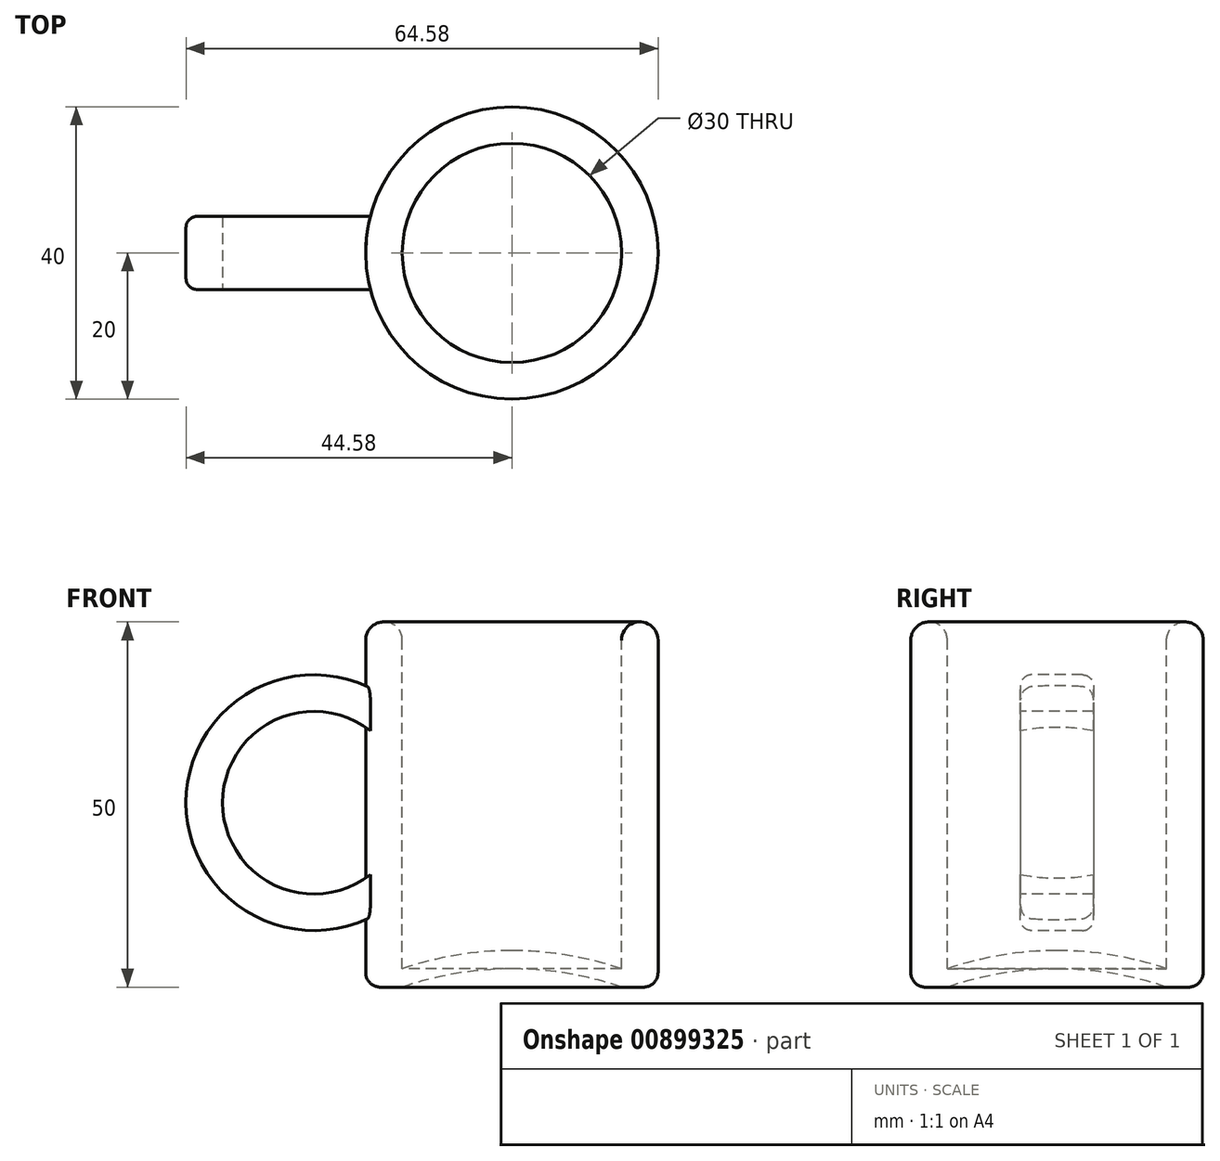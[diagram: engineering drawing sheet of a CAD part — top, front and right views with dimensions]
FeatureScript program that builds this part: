
annotation { "Feature Type Name" : "Feature", "Feature Type Description" : "" }
export const myFeature = defineFeature(function(context is Context, id is Id, definition is map)
    precondition{}
    {
        {
            var Q0;
            Q0=qCreatedBy(makeId("Front.planeOp"),FACE);
            var sketch = newSketch(context, id + "F0", { "sketchPlane" : qUnion([Q0])});
            skLineSegment(sketch, "E0.bottom", {"start": v(0, 0) * mm, "end": v(5, 0) * mm, "construction": true});
            skLineSegment(sketch, "E0.top", {"start": v(0, 47.5) * mm, "end": v(5, 47.5) * mm, "construction": true});
            skLineSegment(sketch, "E0.left", {"start": v(0, 0) * mm, "end": v(0, 47.5) * mm, "construction": true});
            skLineSegment(sketch, "E0.right", {"start": v(40, 0) * mm, "end": v(40, 47.5) * mm});
            skLineSegment(sketch, "E1", {"start": v(5, 47.5) * mm, "end": v(5, 2.5) * mm, "construction": true});
            skLineSegment(sketch, "E2", {"start": v(35, 47.5) * mm, "end": v(35, 2.5) * mm});
            skArc(sketch, "E3", {"start": v(35, 0) * mm, "mid": v(27.6, 1.87) * mm, "end": v(20, 2.5) * mm});
            skLineSegment(sketch, "E4", {"start": v(5, 47.5) * mm, "end": v(20, 47.5) * mm, "construction": true});
            skLineSegment(sketch, "E5", {"start": v(35, 47.5) * mm, "end": v(40, 47.5) * mm});
            skLineSegment(sketch, "E6", {"start": v(35, 0) * mm, "end": v(40, 0) * mm});
            skLineSegment(sketch, "E7", {"start": v(5, 0) * mm, "end": v(20, 0) * mm, "construction": true});
            skArc(sketch, "E8", {"start": v(0, 47.5) * mm, "mid": v(2.5, 50) * mm, "end": v(5, 47.5) * mm, "construction": true});
            skArc(sketch, "E9", {"start": v(35, 47.5) * mm, "mid": v(37.5, 50) * mm, "end": v(40, 47.5) * mm});
            skLineSegment(sketch, "E10", {"start": v(20, 0) * mm, "end": v(20, 2.5) * mm, "construction": true});
            skLineSegment(sketch, "E11", {"start": v(20, 0) * mm, "end": v(35, 0) * mm, "construction": true});
            skLineSegment(sketch, "E12", {"start": v(20, 2.5) * mm, "end": v(20, 5) * mm});
            skLineSegment(sketch, "E13", {"start": v(20, 47.5) * mm, "end": v(35, 47.5) * mm, "construction": true});
            skArc(sketch, "E14", {"start": v(20, 2.5) * mm, "mid": v(12.4, 1.87) * mm, "end": v(5, 0) * mm, "construction": true});
            skLineSegment(sketch, "E15", {"start": v(20, 2.5) * mm, "end": v(20, 2.5) * mm});
            skArc(sketch, "E16", {"start": v(35, 2.5) * mm, "mid": v(27.6, 4.37) * mm, "end": v(20, 5) * mm});
            skLineSegment(sketch, "E17", {"start": v(5, 2.5) * mm, "end": v(5, 2.5) * mm});
            skArc(sketch, "E18", {"start": v(20, 5) * mm, "mid": v(12.4, 4.37) * mm, "end": v(5, 2.5) * mm});
            skLineSegment(sketch, "E19", {"start": v(5, 2.5) * mm, "end": v(5, 0) * mm, "construction": true});
            skLineSegment(sketch, "E20", {"start": v(35, 2.5) * mm, "end": v(35, 0) * mm});
            skLineSegment(sketch, "E21", {"start": v(20, 5) * mm, "end": v(20, 5) * mm});
            skLineSegment(sketch, "E22", {"start": v(20, 5) * mm, "end": v(20, 47.5) * mm, "construction": true});
            skSolve(sketch);
        }
        {
            var Q0;
            Q0 = qSketchRegion(id + "F0", true);
            var Q1;
            Q1=sQuery(id+"F0.wireOp",EDGE,"E10");
            revolve(context, id + "F1", {"surfaceOperationType" : NewSurfaceOperationType.NEW, "entities" : qUnion([Q0]), "axis" : qUnion([Q1]), "revolveType" : RevolveType.FULL, "oppositeDirection" : true});
        }
        {
            var Q0;
            Q0=qCreatedBy(makeId("Front.planeOp"),FACE);
            var sketch = newSketch(context, id + "F2", { "sketchPlane" : qUnion([Q0])});
            skPoint(sketch, "E23.0", {"position": v(0, 0) * mm});
            skLineSegment(sketch, "E24", {"start": v(40, 47.5) * mm, "end": v(40, 0) * mm});
            skLineSegment(sketch, "E25", {"start": v(0, 0) * mm, "end": v(0, 47.5) * mm, "construction": true});
            skLineSegment(sketch, "E26", {"start": v(1.5, 0) * mm, "end": v(1.5, 10) * mm, "construction": true});
            skLineSegment(sketch, "E27", {"start": v(1.5, 47.5) * mm, "end": v(0, 47.5) * mm});
            skLineSegment(sketch, "E28", {"start": v(1.5, 40.5) * mm, "end": v(1.5, 47.5) * mm, "construction": true});
            skLineSegment(sketch, "E29", {"start": v(1.5, 34.34) * mm, "end": v(1.5, 40.5) * mm});
            skLineSegment(sketch, "E30", {"start": v(1.5, 16.16) * mm, "end": v(1.5, 34.34) * mm, "construction": true});
            skLineSegment(sketch, "E31", {"start": v(1.5, 10) * mm, "end": v(1.5, 16.16) * mm});
            skArc(sketch, "E32", {"start": v(1.5, 40.5) * mm, "mid": v(-24.58, 25.25) * mm, "end": v(1.5, 10) * mm});
            skArc(sketch, "E33", {"start": v(1.5, 34.34) * mm, "mid": v(-19.58, 25.25) * mm, "end": v(1.5, 16.16) * mm});
            skSolve(sketch);
        }
        {
            var Q0;
            {var subQ0=sQuery(id+"F2.wireOp",EDGE,"zNirZaeI-mv0y-j9wX-MBT8-WwsDXe8e62ri");Q0=makeQuery(id+"F2.imprint","IMPRINT",FACE,{"disambiguationData":[TD([[makeQuery(id+"F2.imprint","IMPRINT",EDGE,{"derivedFrom":subQ0}),1.0]])]});}
            var Q1;
            Q1=makeQuery(id+"F2.imprint","IMPRINT",FACE,{"disambiguationData":[TD([[makeQuery(id+"F2.imprint","IMPRINT",EDGE,{"derivedFrom":sQuery(id+"F2.wireOp",EDGE,"E29")}),1.0]])]});
            extrude(context, id + "F3", {"entities" : qUnion([Q0, Q1]), "operationType" : NewBodyOperationType.ADD, "endBound" : BoundingType.SYMMETRIC, "oppositeDirection" : true, "depth" : 10 * mm, "offsetDistance" : 25 * mm});
        }
        {
            var Q0;
            Q0=makeQuery(id+"F3.opExtrude","CAP_EDGE",EDGE,{"disambiguationData":[OSD([sQuery(id+"F2.wireOp",EDGE,"E32")])],"isStart":false});
            var Q1;
            Q1=makeQuery(id+"F3.opExtrude","CAP_EDGE",EDGE,{"disambiguationData":[OSD([sQuery(id+"F2.wireOp",EDGE,"E32")])],"isStart":true});
            fillet(context, id + "F4", {"entities" : qUnion([Q0, Q1]), "radius" : 1.5 * mm, "tangentPropagation" : true, "allowEdgeOverflow" : false});
        }
        {
            var Q0;
            Q0=makeQuery(id+"F1.opRevolve","SWEPT_EDGE",EDGE,{"disambiguationData":[OSD([sQuery(id+"F0.wireOp",EDGE,"E0.right"),sQuery(id+"F0.wireOp",EDGE,"E6")])]});
            fillet(context, id + "F5", {"entities" : qUnion([Q0]), "radius" : 2 * mm, "tangentPropagation" : true, "allowEdgeOverflow" : false});
        }
    });
